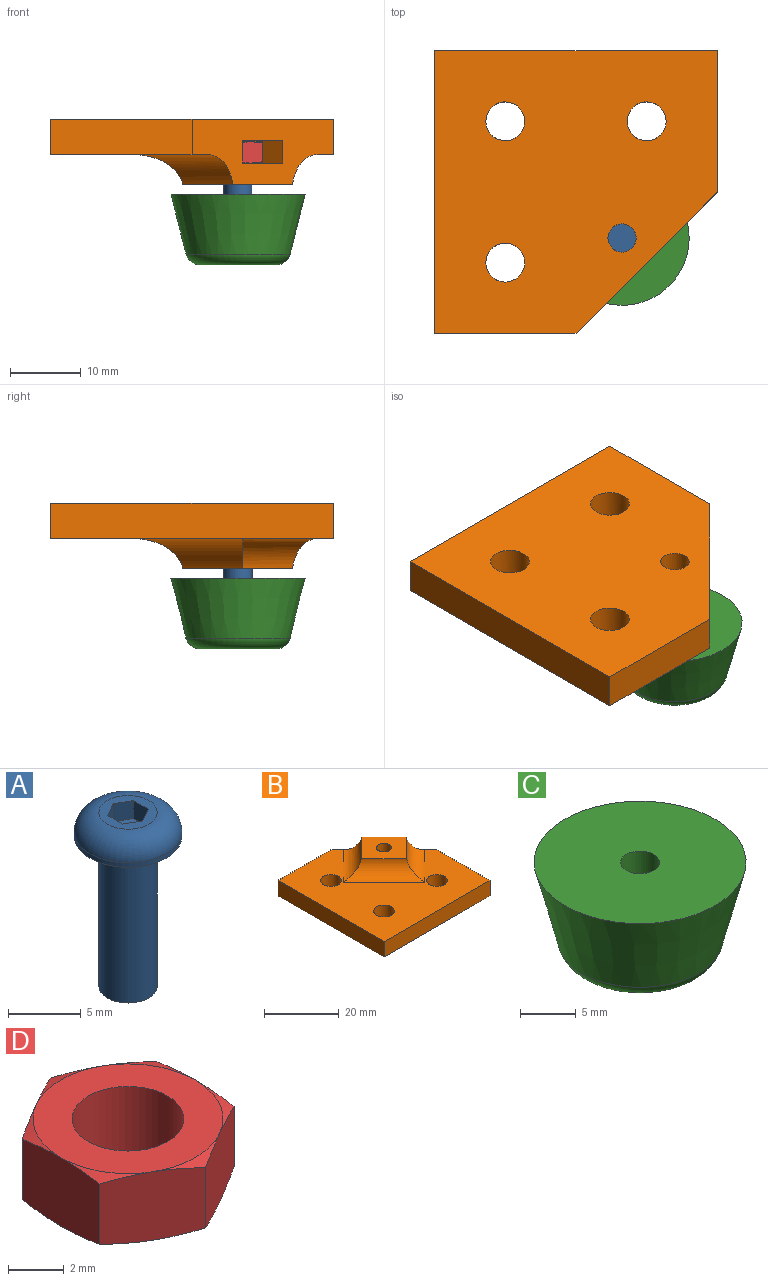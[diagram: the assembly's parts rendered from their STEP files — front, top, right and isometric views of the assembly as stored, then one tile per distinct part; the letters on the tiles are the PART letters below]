
ASSEMBLY  parts=4 mates=3
PART A: 14 faces, bbox 8x8x14.6 mm
  f0: plane 4x4mm, normal (0,0,1), area 7.2mm2, adj f2,f6,f7,f8,f9,f10,f11
  f1: cylinder r=3.7mm len=7.4mm, axis (0,0,1), area 8.8mm2, adj f2,f5
  f2: torus R=2mm, axis (0,0,1), area 49.9mm2, adj f0,f1
  f3: cylinder r=2mm len=12.4mm, axis (0,0,1), area 155.8mm2, adj f4,f13
  f4: torus R=2.2mm, axis (0,0,1), area 4.1mm2, adj f3,f5
  f5: plane 7.4x7.4mm, normal (0,0,-1), area 27.8mm2, adj f1,f4
  f6: plane 1.5x1.25mm, normal (-0.5,-0.87,0), area 2.2mm2, adj f0,f7,f11,f12
  f7: plane 1.5x1.25mm, normal (0.5,-0.87,0), area 2.2mm2, adj f0,f6,f8,f12
  f8: plane 1.5x1.44mm, normal (1,0,0), area 2.2mm2, adj f0,f7,f9,f12
  f9: plane 1.5x1.25mm, normal (0.5,0.87,0), area 2.2mm2, adj f0,f8,f10,f12
  f10: plane 1.5x1.25mm, normal (-0.5,0.87,0), area 2.2mm2, adj f0,f9,f11,f12
  f11: plane 1.5x1.44mm, normal (-1,0,0), area 2.2mm2, adj f0,f6,f10,f12
  f12: plane 2.89x2.5mm, normal (0,0,1), area 5.4mm2, adj f6,f7,f8,f9,f10,f11
  f13: plane 4x4mm, normal (0,0,-1), area 12.6mm2, adj f3
PART B: 23 faces, bbox 40x40x9.2 mm
  f0: cylinder r=2mm len=4mm, axis (0,0,-1), area 37.7mm2, adj f8,f22
  f1: plane 40x40mm, normal (0,0,1), area 1002.1mm2, adj f2,f3,f4,f5,f6,f10,f11,f12
  f2: plane 40x5mm, normal (-1,0,0), area 200mm2, adj f1,f3,f6,f8
  f3: plane 40x5mm, normal (0,-1,0), area 200mm2, adj f1,f2,f4,f8
  f4: plane 20x5mm, normal (1,0,0), area 100mm2, adj f1,f3,f5,f8
  f5: plane 20x20mm, normal (0.71,0.71,0), area 176.1mm2, adj f1,f4,f6,f8,f9,f10,f12,f17
  f6: plane 20x5mm, normal (0,1,0), area 100mm2, adj f1,f2,f5,f8
  f7: cylinder r=2mm len=4mm, axis (0,0,-1), area 37.7mm2, adj f9,f21
  f8: plane 40x40mm, normal (0,0,-1), area 1316.2mm2, adj f0,f2,f3,f4,f5,f6,f13,f14
  f9: plane 15.56x15.56mm, normal (0,0,1), area 107.4mm2, adj f5,f7,f10,f11,f12
  f10: cylinder r=5mm len=14.05mm, axis (-0.71,-0.71,0), area 84.3mm2, adj f1,f5,f9,f11
  f11: cylinder r=5mm len=18.96mm, axis (-0.71,0.71,0), area 112.2mm2, adj f1,f9,f10,f12
  f12: cylinder r=5mm len=14.05mm, axis (0.71,0.71,0), area 84.3mm2, adj f1,f5,f9,f11
  f13: cylinder r=2.75mm len=5.5mm, axis (0,0,-1), area 86.4mm2, adj f1,f8
  f14: cylinder r=2.75mm len=5.5mm, axis (0,0,-1), area 86.4mm2, adj f1,f8
  f15: cylinder r=2.75mm len=5.5mm, axis (0,0,-1), area 86.4mm2, adj f1,f8
  f16: plane 3.91x3.2mm, normal (-0.26,0.97,0), area 13mm2, adj f17,f20,f21,f22
  f17: plane 3.54x3.54mm, normal (-0.71,0.71,0), area 16mm2, adj f5,f16,f21,f22
  f18: plane 3.54x3.54mm, normal (0.71,-0.71,0), area 16mm2, adj f5,f19,f21,f22
  f19: plane 3.91x3.2mm, normal (0.97,-0.26,0), area 13mm2, adj f18,f20,f21,f22
  f20: plane 3.2x2.86mm, normal (0.71,0.71,0), area 13mm2, adj f16,f19,f21,f22
  f21: plane 10.31x10.31mm, normal (0,0,-1), area 49.2mm2, adj f5,f7,f16,f17,f18,f19,f20
  f22: plane 10.31x10.31mm, normal (0,0,1), area 49.2mm2, adj f0,f5,f16,f17,f18,f19,f20
PART C: 7 faces, bbox 19x19x10 mm
  f0: plane 7.5x7.5mm, normal (0,0,-1), area 34.6mm2, adj f1,f6
  f1: cylinder r=3.75mm len=7.5mm, axis (0,0,1), area 117.8mm2, adj f0,f2
  f2: plane 10.88x10.88mm, normal (0,0,-1), area 48.7mm2, adj f1,f3
  f3: torus R=5.44mm, axis (0,0,1), area 109.6mm2, adj f2,f4
  f4: cone r=9.5mm half-angle=14deg, axis (0,0,1), area 463.8mm2, adj f3,f5
  f5: plane 19x19mm, normal (0,0,1), area 273.9mm2, adj f4,f6
  f6: cylinder r=1.75mm len=5mm, axis (0,0,1), area 55mm2, adj f0,f5
PART D: 21 faces, bbox 8.1x8.1x3.3 mm
  f0: cone r=3.4mm half-angle=71.1deg, axis (0,0,-1), area 1mm2, adj f11,f15,f20
  f1: cone r=3.4mm half-angle=71.1deg, axis (0,0,-1), area 1mm2, adj f11,f15,f16
  f2: cone r=3.4mm half-angle=71.1deg, axis (0,0,-1), area 1mm2, adj f11,f16,f17
  f3: cone r=3.4mm half-angle=71.1deg, axis (0,0,-1), area 1mm2, adj f11,f17,f18
  f4: cone r=3.4mm half-angle=71.1deg, axis (0,0,-1), area 1mm2, adj f11,f18,f19
  f5: cone r=3.4mm half-angle=71.1deg, axis (0,0,1), area 1mm2, adj f13,f15,f20
  f6: cone r=3.4mm half-angle=71.1deg, axis (0,0,1), area 1mm2, adj f13,f15,f16
  f7: cone r=3.4mm half-angle=71.1deg, axis (0,0,1), area 1mm2, adj f13,f16,f17
  f8: cone r=3.4mm half-angle=71.1deg, axis (0,0,1), area 1mm2, adj f13,f17,f18
  f9: cone r=3.4mm half-angle=71.1deg, axis (0,0,1), area 1mm2, adj f13,f18,f19
  f10: cone r=3.4mm half-angle=71.1deg, axis (0,0,-1), area 1mm2, adj f11,f19,f20
  f11: plane 6.8x6.8mm, normal (0,0,1), area 23.8mm2, adj f0,f1,f2,f3,f4,f10,f12
  f12: cylinder r=2mm len=4mm, axis (0,0,-1), area 37.7mm2, adj f11,f13
  f13: plane 6.8x6.8mm, normal (0,0,-1), area 23.8mm2, adj f5,f6,f7,f8,f9,f12,f14
  f14: cone r=3.4mm half-angle=71.1deg, axis (0,0,1), area 1mm2, adj f13,f19,f20
  f15: plane 3.7x3.3mm, normal (0.5,0.87,0), area 11.3mm2, adj f0,f1,f5,f6,f16,f20
  f16: plane 3.7x3.3mm, normal (-0.5,0.87,0), area 11.3mm2, adj f1,f2,f6,f7,f15,f17
  f17: plane 4.23x3.3mm, normal (-1,0,0), area 11.3mm2, adj f2,f3,f7,f8,f16,f18
  f18: plane 3.7x3.3mm, normal (-0.5,-0.87,0), area 11.3mm2, adj f3,f4,f8,f9,f17,f19
  f19: plane 3.7x3.3mm, normal (0.5,-0.87,0), area 11.3mm2, adj f4,f9,f10,f14,f18,f20
  f20: plane 4.23x3.3mm, normal (1,0,0), area 11.3mm2, adj f0,f5,f10,f14,f15,f19
PLACE A rot(axis=(0,-1,0),180deg) t=(30.2,24.03,-6.52)mm
PLACE B rot(axis=(1,0,0),180deg) t=(3.68,10.55,11.08)mm
PLACE C t=(30.2,-15.97,0.48)mm
PLACE D rot(axis=(-1,0,0),180deg) t=(55.2,-0.97,7.7)mm
MATE fastened D.f0 <-> B.f0  axis (0,0,-1) through (30.2,-15.97,4.88)mm
MATE fastened A.f1 <-> C.f1  axis (0,0,1) through (30.2,-15.97,-4.52)mm
MATE fastened A.f1 <-> B.f0  axis (0,0,1) through (30.2,-15.97,8.08)mm
